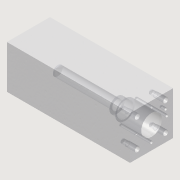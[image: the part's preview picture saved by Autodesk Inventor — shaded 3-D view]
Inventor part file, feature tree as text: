
AUTODESK INVENTOR PART (.ipt)
format: ipt  version: 2014 (Build 180170000, 170)  size: 345,088 bytes
history: native  units: mm
features: other x48, extrude x21, sketch x21
ambient origin geometry x8: Origin, YZ Plane, XZ Plane, XY Plane, X Axis, Y Axis, Z Axis, Center Point
bodies: 实体1 (feature_tree)
feature tree (90):
  extrude  "拉伸1"  Depth=33.7mm
  other  "UCS1"
  other  "UCS2"
  other  "UCS3"
  other  "UCS4"
  other  "UCS5"
  other  "UCS6"
  extrude  "拉伸23"  Depth=35.0mm
  extrude  "拉伸24"  Depth=65.0mm
  extrude  "拉伸25"  Depth=10.0mm
  extrude  "拉伸26"  Depth=43.0mm
  extrude  "拉伸28"  Depth=13.0mm
  extrude  "拉伸29"  Depth=16.0mm
  extrude  "拉伸30"  Depth=152.4mm
  extrude  "拉伸31"  Depth=23.0mm
  extrude  "拉伸32"  Depth=23.0mm
  extrude  "拉伸33"  Depth=23.0mm
  extrude  "拉伸34"  Depth=23.0mm
  extrude  "拉伸35"  Depth=24.0mm TaperAngle=0.0deg
  extrude  "拉伸36"  Depth=24.0mm
  extrude  "拉伸37"  Depth=200.0mm
  extrude  "拉伸38"  Depth=8.0mm
  extrude  "拉伸39"  Depth=16.0mm TaperAngle=0.0deg
  extrude  "拉伸40"  Depth=4.0mm
  extrude  "拉伸41"  Depth=4.0mm
  extrude  "拉伸42"  TaperAngle=0.0deg  [1 undecoded]
  extrude  "拉伸43"  TaperAngle=0.0deg  [1 undecoded]
  sketch  "草图1"  dims[d0=70.0mm d1=0.0mm]
  sketch  "草图27"  dims[d2=0.0mm d3=0.0mm d4=0.0mm d5=0.0mm d6=0.0mm d7=0.0mm]
  sketch  "草图28"  dims[d8=0.0mm d9=0.0mm d10=0.0mm d11=0.0mm d12=0.0mm d13=0.0mm]
  sketch  "草图29"  dims[d14=0.0mm d15=0.0mm d16=0.0mm d17=0.0mm d18=0.0mm d19=0.0mm]
  sketch  "草图31"  dims[d20=0.0mm d21=0.0mm d22=0.0mm d23=0.0mm d24=0.0mm d25=0.0mm]
  sketch  "草图32"  dims[d26=0.0mm d27=0.0mm d28=0.0mm d29=0.0mm d30=0.0mm d31=0.0mm]
  sketch  "草图33"  dims[d32=0.0mm d33=0.0mm d34=0.0mm d35=0.0mm d36=0.0mm d37=0.0mm d110=33.7mm]
  sketch  "草图34"  dims[d111=36.0mm d112=35.0mm]
  sketch  "草图35"  dims[d113=65.0mm d114=65.0mm]
  sketch  "草图36"  dims[d115=10.0mm d116=-2.617994mm d117=32.0mm]
  sketch  "草图37"  dims[d118=43.0mm d119=0.0mm d120=26.07mm]
  sketch  "草图38"  dims[d121=13.0mm d122=-2.617994mm d124=25.0mm]
  sketch  "草图39"  dims[d125=56.0mm d126=0.0mm d127=16.0mm]
  sketch  "草图40"  dims[d130=152.4mm d131=0.0mm d132=152.4mm d133=-10.297443mm]
  sketch  "草图41"  dims[d134=6.75mm d135=23.0mm]
  sketch  "草图42"  dims[d136=23.0mm d137=23.0mm]
  sketch  "草图43"  dims[d138=23.0mm d139=23.0mm]
  sketch  "草图44"  dims[d140=23.0mm d141=23.0mm]
  sketch  "草图45"  dims[d142=23.0mm d143=24.0mm d144=0.0mm]
  sketch  "草图46"  dims[d145=24.0mm d146=-10.297443mm d147=24.0mm d148=-10.297443mm]
  sketch  "草图47"  dims[d149=24.0mm d150=-10.297443mm d151=24.0mm d152=-10.297443mm d153=8.0mm d154=16.0mm d155=0.0mm d156=4.0mm d157=4.0mm d160=0.0mm d161=0.0mm d162=25.0mm d163=25.000195mm d164=25.4mm d165=0.0mm d166=25.4mm d167=-10.297443mm d168=25.4mm d169=-10.297443mm d170=4.0mm d171=4.0mm d172=25.0mm d173=0.0mm d174=25.0mm d175=0.0mm d176=25.4mm d177=0.0mm d178=25.4mm d179=-10.297443mm d180=25.4mm d181=-10.297443mm d182=4.0mm d183=23.0mm d184=10.5mm d185=8.0mm d186=0.0mm d187=8.0mm d188=-10.297443mm d294=70.0mm d295=200.0mm]
  other  "UCS1: YZ 平面"
  other  "UCS1: XZ 平面"
  other  "UCS1: XY 平面"
  other  "UCS1: X 轴"
  other  "UCS1: Y 轴"
  other  "UCS1: Z 轴"
  other  "UCS1: 原点"
  other  "UCS2: YZ 平面"
  other  "UCS2: XZ 平面"
  other  "UCS2: XY 平面"
  other  "UCS2: X 轴"
  other  "UCS2: Y 轴"
  other  "UCS2: Z 轴"
  other  "UCS2: 原点"
  other  "UCS3: YZ 平面"
  other  "UCS3: XZ 平面"
  other  "UCS3: XY 平面"
  other  "UCS3: X 轴"
  other  "UCS3: Y 轴"
  other  "UCS3: Z 轴"
  other  "UCS3: 原点"
  other  "UCS4: YZ 平面"
  other  "UCS4: XZ 平面"
  other  "UCS4: XY 平面"
  other  "UCS4: X 轴"
  other  "UCS4: Y 轴"
  other  "UCS4: Z 轴"
  other  "UCS4: 原点"
  other  "UCS5: YZ 平面"
  other  "UCS5: XZ 平面"
  other  "UCS5: XY 平面"
  other  "UCS5: X 轴"
  other  "UCS5: Y 轴"
  other  "UCS5: Z 轴"
  other  "UCS5: 原点"
  other  "UCS6: YZ 平面"
  other  "UCS6: XZ 平面"
  other  "UCS6: XY 平面"
  other  "UCS6: X 轴"
  other  "UCS6: Y 轴"
  other  "UCS6: Z 轴"
  other  "UCS6: 原点"
note: 2 required parameter values undecoded (feature->parameter linkage not recoverable at this tier; creation-order binding heuristic only, values carry confidence <= 0.55)
